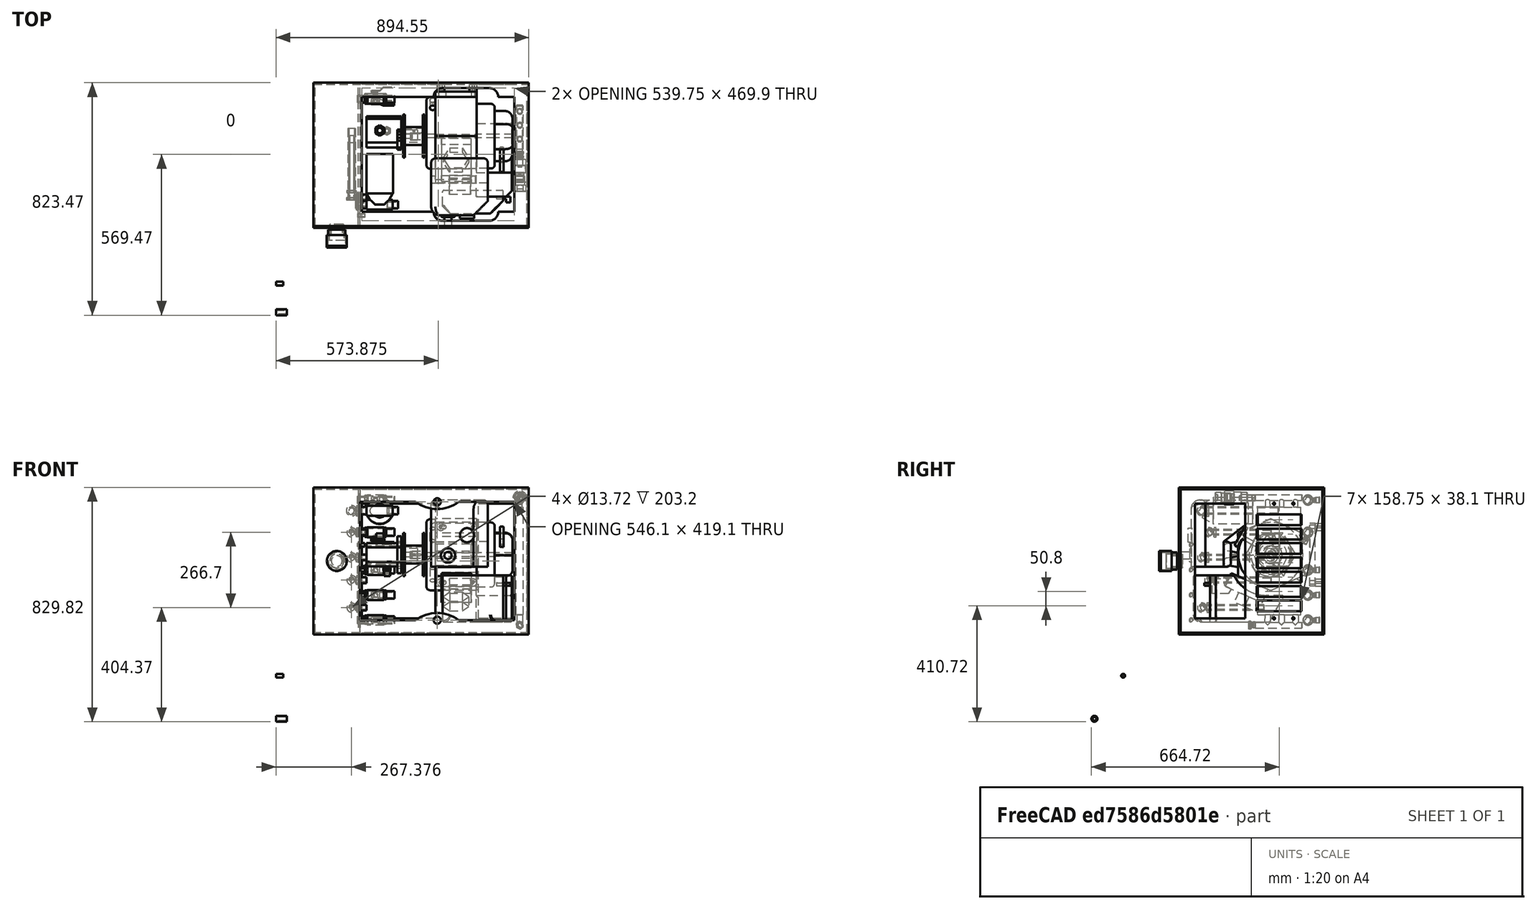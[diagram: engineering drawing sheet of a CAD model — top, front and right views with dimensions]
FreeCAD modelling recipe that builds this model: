
FCSTD DOCUMENT  (FreeCAD 0.16R6712 (Git))
Label: powercube v17.11_plumbing
License: CreativeCommons Attribution-ShareAlike
LicenseURL: http://creativecommons.org/licenses/by-sa/4.0/
objects: App::FeaturePython×29, Part::FeaturePython×17, Part::Feature×9, Part::Part2DObjectPython×4, App::DocumentObjectGroup×3
note: 30 computed .brp shape members not serialized (recipe doc carries the construction recipe); baked Part::Feature solids carry a one-line shape summary decoded from their .brp

FEATURE [Part::Feature] Cut002  label="0.75 NPT x 1.5in pipe section"
  Placement = pos=(-71.1581,-527.05,186.267) rot=(0,-1,0;1.5708rad)
  shape: bbox 38.1 x 26.67 x 26.67 mm, 4 faces (baked)
FEATURE [Part::Feature] Pad005  label="1/4" NPT pipe"
  Placement = pos=(-152.4,-203.2,-152.4) rot=(0.57735,0.57735,0.57735;2.0944rad)
  shape: bbox 25.4 x 13.72 x 13.72 mm, 4 faces (baked)
FEATURE [Part::FeaturePython] Clone039  label="Clone of 0.75 NPT x 1.5in pipe section005"  # Draft clone (typed FeaturePython)
  Objects = -> [Cut002]
  Placement = pos=(229.07,450.85,44.45) rot=(0,1,0;1.5708rad)
  Scale = (1,1,1)
FEATURE [Part::FeaturePython] Clone040  label="Clone of 0.75 NPT x 1.5in pipe section006"  # Draft clone (typed FeaturePython)
  Objects = -> [Cut002]
  Placement = pos=(229.07,450.85,133.35) rot=(0,1,0;1.5708rad)
  Scale = (1,1,1)
FEATURE [Part::FeaturePython] Clone041  label="Clone of 0.75 NPT x 1.5in pipe section007"  # Draft clone (typed FeaturePython)
  Objects = -> [Cut002]
  Placement = pos=(229.07,450.85,222.25) rot=(0,1,0;1.5708rad)
  Scale = (1,1,1)
FEATURE [Part::FeaturePython] Clone042  label="Clone of 0.75 NPT x 1.5in pipe section008"  # Draft clone (typed FeaturePython)
  Objects = -> [Cut002]
  Placement = pos=(229.07,450.85,355.6) rot=(0,1,0;1.5708rad)
  Scale = (1,1,1)
FEATURE [Part::FeaturePython] Clone043  label="Clone of 0.75 NPT x 1.5in pipe section009"  # Draft clone (typed FeaturePython)
  Objects = -> [Cut002]
  Placement = pos=(229.07,450.85,469.9) rot=(0,1,0;1.5708rad)
  Scale = (1,1,1)
FEATURE [Part::Feature] Pad006  label="engine rubber feet"
  Placement = pos=(-254,-203.2,254) rot=(1,0,0;1.5708rad)
  shape: bbox 25.4 x 25.4 x 25.4 mm, 4 faces (baked)
FEATURE [Part::FeaturePython] PC_1708_oil_filter_002  # a2plus imported part (geometry in sourceFile) (typed FeaturePython)
  Placement = pos=(214.465,115.824,431.8) rot=(1,0,0;1.5708rad)
  fixedPosition = false
  sourceFile = <userpath>/Documents/Freecad docs/Power Cube/PC_1708_oil_filter.fcstd
  timeLastImport = 0
  updateColors = true
FEATURE [Part::FeaturePython] Clone053  label="Clone of 0.75 NPT x 1.5in pipe section010"  # Draft clone (typed FeaturePython)
  Objects = -> [Cut002]
  Placement = pos=(241.77,76.2,431.8) rot=(0,1,0;1.5708rad)
  Scale = (1,1,1)
FEATURE [App::FeaturePython] circularEdgeConstraint35  label="circularEdgeConstraint35__PC_1708_oil_filter_002"  # a2plus constraint (typed FeaturePython)
  Object1 = Clone053
  Object2 = PC_1708_oil_filter_002
  SubElement1 = Edge3
  SubElement2 = Edge17
  Type = circularEdge
  directionConstraint = 0
  lockRotation = false
  offset = -19.05
FEATURE [App::FeaturePython] circularEdgeConstraint35_mirror  label="circularEdgeConstraint35__Clone of 0.75 NPT x 1.5in pipe section010"  # a2plus constraint (typed FeaturePython)
  Object1 = Clone053
  Object2 = PC_1708_oil_filter_002
  SubElement1 = Edge3
  SubElement2 = Edge17
  Type = circularEdge
  directionConstraint = 0
  lockRotation = false
  offset = -19.05
FEATURE [Part::Feature] Fusion001001  label="1240_cooler_and_fittings001"
  Placement = pos=(637.3,546.25,-104.8) rot=(0.57735,-0.57735,-0.57735;2.0944rad)
  shape: bbox 48 x 306.6 x 489 mm, 154 faces, 3 solids (baked)
FEATURE [Part::Feature] Pad001  label="0.5in x 1.5in NPT"
  Placement = pos=(-152.4,-304.8,-304.8) rot=(0.57735,0.57735,0.57735;2.0944rad)
  shape: bbox 38.1 x 21.34 x 21.34 mm, 4 faces (baked)
FEATURE [Part::FeaturePython] PC_v17_11_Frame_simple_01  # a2plus imported part (geometry in sourceFile) (typed FeaturePython)
  fixedPosition = true
  sourceFile = <userpath>/Documents/Power Cube v17.11/PC v17.11 Frame simple.fcstd
  timeLastImport = 1.53306e+09
  updateColors = true
FEATURE [App::DocumentObjectGroup] Group  label="Frame"
  Group = -> [PC_v17_11_Frame_simple_01]
FEATURE [Part::FeaturePython] Clone  label="Clone of engine rubber feet"  # Draft clone (typed FeaturePython)
  Objects = -> [Pad006]
  Placement = pos=(431,501.65,177.8) rot=(1,0,0;1.5708rad)
  Scale = (1,1,1)
FEATURE [Part::FeaturePython] Clone070  label="Clone of engine rubber feet001"  # Draft clone (typed FeaturePython)
  Objects = -> [Pad006]
  Placement = pos=(545.3,501.65,177.8) rot=(1,0,0;1.5708rad)
  Scale = (1,1,1)
FEATURE [Part::FeaturePython] Clone071  label="Clone of engine rubber feet002"  # Draft clone (typed FeaturePython)
  Objects = -> [Pad006]
  Placement = pos=(545.3,501.65,374.65) rot=(1,0,0;1.5708rad)
  Scale = (1,1,1)
FEATURE [Part::FeaturePython] Clone072  label="Clone of engine rubber feet003"  # Draft clone (typed FeaturePython)
  Objects = -> [Pad006]
  Placement = pos=(431,501.65,374.65) rot=(1,0,0;1.5708rad)
  Scale = (1,1,1)
FEATURE [App::FeaturePython] circularEdgeConstraint01  label="circularEdgeConstraint01__PC_v17_11_Frame_simple_01"  # a2plus constraint (typed FeaturePython)
  Object1 = Clone
  Object2 = PC_v17_11_Frame_simple_01
  SubElement1 = Edge5
  SubElement2 = Edge252
  Type = circularEdge
  directionConstraint = 0
  lockRotation = false
  offset = 0
FEATURE [App::FeaturePython] circularEdgeConstraint01_mirror  label="circularEdgeConstraint01__Clone of engine rubber feet"  # a2plus constraint (typed FeaturePython)
  Object1 = Clone
  Object2 = PC_v17_11_Frame_simple_01
  SubElement1 = Edge5
  SubElement2 = Edge252
  Type = circularEdge
  directionConstraint = 0
  lockRotation = false
  offset = 0
FEATURE [App::FeaturePython] circularEdgeConstraint02  label="circularEdgeConstraint02__Clone of engine rubber feet001"  # a2plus constraint (typed FeaturePython)
  Object1 = PC_v17_11_Frame_simple_01
  Object2 = Clone070
  SubElement1 = Edge249
  SubElement2 = Edge5
  Type = circularEdge
  directionConstraint = 0
  lockRotation = false
  offset = 0
FEATURE [App::FeaturePython] circularEdgeConstraint02_mirror  label="circularEdgeConstraint02__PC_v17_11_Frame_simple_01"  # a2plus constraint (typed FeaturePython)
  Object1 = PC_v17_11_Frame_simple_01
  Object2 = Clone070
  SubElement1 = Edge249
  SubElement2 = Edge5
  Type = circularEdge
  directionConstraint = 0
  lockRotation = false
  offset = 0
FEATURE [App::FeaturePython] circularEdgeConstraint03  label="circularEdgeConstraint03__PC_v17_11_Frame_simple_01"  # a2plus constraint (typed FeaturePython)
  Object1 = Clone071
  Object2 = PC_v17_11_Frame_simple_01
  SubElement1 = Edge5
  SubElement2 = Edge243
  Type = circularEdge
  directionConstraint = 0
  lockRotation = false
  offset = 0
FEATURE [App::FeaturePython] circularEdgeConstraint03_mirror  label="circularEdgeConstraint03__Clone of engine rubber feet002"  # a2plus constraint (typed FeaturePython)
  Object1 = Clone071
  Object2 = PC_v17_11_Frame_simple_01
  SubElement1 = Edge5
  SubElement2 = Edge243
  Type = circularEdge
  directionConstraint = 0
  lockRotation = false
  offset = 0
FEATURE [App::FeaturePython] circularEdgeConstraint04  label="circularEdgeConstraint04__Clone of engine rubber feet003"  # a2plus constraint (typed FeaturePython)
  Object1 = PC_v17_11_Frame_simple_01
  Object2 = Clone072
  SubElement1 = Edge246
  SubElement2 = Edge5
  Type = circularEdge
  directionConstraint = 0
  lockRotation = false
  offset = 0
FEATURE [App::FeaturePython] circularEdgeConstraint04_mirror  label="circularEdgeConstraint04__PC_v17_11_Frame_simple_01"  # a2plus constraint (typed FeaturePython)
  Object1 = PC_v17_11_Frame_simple_01
  Object2 = Clone072
  SubElement1 = Edge246
  SubElement2 = Edge5
  Type = circularEdge
  directionConstraint = 0
  lockRotation = false
  offset = 0
FEATURE [App::DocumentObjectGroup] Group001  label="Power"
  Group = -> [Pad006,Clone,Clone070,Clone071,Clone072,circularEdgeConstraint01,circularEdgeConstraint02_mirror,circularEdgeConstraint03,circularEdgeConstraint04_mirror]
FEATURE [App::FeaturePython] circularEdgeConstraint06_mirror  label="circularEdgeConstraint06__Clone of 1/4" NPT pipe"  # a2plus constraint (typed FeaturePython)
  Object1 = Clone073
  Object2 = PC_v17_11_Frame_simple_01
  SubElement1 = Edge6
  SubElement2 = Edge81
  Type = circularEdge
  directionConstraint = 1
  lockRotation = false
  offset = 0
FEATURE [App::DocumentObjectGroup] Group002  label="Plumbing"
  Group = -> [Pad001,Fusion001001,Cut002,Pad005,Clone039,Clone040,Clone041,Clone042,Clone043,PC_1708_oil_filter_002,Clone053,circularEdgeConstraint35,circularEdgeConstraint06_mirror]
FEATURE [Part::Feature] Compound002001  label="0.75in NPT Ball Valve"
  Placement = pos=(812.8,-175.26,330.2) rot=(-0.57735,-0.57735,-0.57735;2.0944rad)
  shape: bbox 104 x 60.2 x 35.56 mm, 53 faces, 5 solids (baked)
FEATURE [Part::FeaturePython] Clone077  label="Clone of 0.75in NPT Ball Valve"  # Draft clone (typed FeaturePython)
  Objects = -> [Compound002001]
  Placement = pos=(237.96,440.69,44.45) rot=(0.57735,0.57735,0.57735;4.18879rad)
  Scale = (1,1,1)
FEATURE [Part::FeaturePython] Clone078  label="Clone of 0.75in NPT Ball Valve001"  # Draft clone (typed FeaturePython)
  Objects = -> [Compound002001]
  Placement = pos=(237.96,440.69,133.35) rot=(0.57735,0.57735,0.57735;4.18879rad)
  Scale = (1,1,1)
FEATURE [Part::FeaturePython] Clone079  label="Clone of 0.75in NPT Ball Valve002"  # Draft clone (typed FeaturePython)
  Objects = -> [Compound002001]
  Placement = pos=(237.96,440.69,222.25) rot=(0.57735,0.57735,0.57735;4.18879rad)
  Scale = (1,1,1)
FEATURE [Part::FeaturePython] Clone080  label="Clone of 0.75in NPT Ball Valve003"  # Draft clone (typed FeaturePython)
  Objects = -> [Compound002001]
  Placement = pos=(237.96,454.305,365.155) rot=(0.701739,0.701739,-0.122979;2.89686rad)
  Scale = (1,1,1)
FEATURE [Part::FeaturePython] Clone081  label="Clone of 0.75in NPT Ball Valve004"  # Draft clone (typed FeaturePython)
  Objects = -> [Compound002001]
  Placement = pos=(237.96,440.69,469.9) rot=(0.57735,0.57735,0.57735;4.18879rad)
  Scale = (1,1,1)
FEATURE [App::FeaturePython] circularEdgeConstraint26  # a2plus constraint (typed FeaturePython)
  Object1 = Clone039
  Object2 = Clone077
  SubElement1 = Edge3
  SubElement2 = Edge59
  Type = circularEdge
  directionConstraint = 0
  lockRotation = false
  offset = -8.89
FEATURE [App::FeaturePython] circularEdgeConstraint27  # a2plus constraint (typed FeaturePython)
  Object1 = Clone040
  Object2 = Clone078
  SubElement1 = Edge3
  SubElement2 = Edge59
  Type = circularEdge
  directionConstraint = 0
  lockRotation = false
  offset = -8.89
FEATURE [App::FeaturePython] circularEdgeConstraint28  # a2plus constraint (typed FeaturePython)
  Object1 = Clone041
  Object2 = Clone079
  SubElement1 = Edge3
  SubElement2 = Edge59
  Type = circularEdge
  directionConstraint = 0
  lockRotation = false
  offset = -8.89
FEATURE [App::FeaturePython] circularEdgeConstraint30  # a2plus constraint (typed FeaturePython)
  Object1 = Clone043
  Object2 = Clone081
  SubElement1 = Edge3
  SubElement2 = Edge59
  Type = circularEdge
  directionConstraint = 0
  lockRotation = false
  offset = -8.89
FEATURE [Part::Feature] Compound002002002005003  label="engine_pump_module"
  Placement = pos=(297.65,744.033,-100.328) rot=(0,0,1;0rad)
  shape: bbox 517.5 x 482.5 x 432.2 mm, 345 faces, 25 solids (baked)
FEATURE [App::FeaturePython] circularEdgeConstraint05  label="cEc05_engine_module_vertical"  # a2plus constraint (typed FeaturePython)
  Object1 = Compound002002002005003
  Object2 = Clone071
  SubElement1 = Edge773
  SubElement2 = Edge6
  Type = circularEdge
  directionConstraint = 1
  lockRotation = false
  offset = 0
FEATURE [App::FeaturePython] circularEdgeConstraint06  label="circularEdgeConstraint06__PC_v17_11_Frame_simple_01"  # a2plus constraint (typed FeaturePython)
  Object1 = Clone081
  Object2 = PC_v17_11_Frame_simple_01
  SubElement1 = Edge72
  SubElement2 = Edge91
  Type = circularEdge
  directionConstraint = 0
  lockRotation = false
  offset = -12.7
FEATURE [App::FeaturePython] circularEdgeConstraint06_mirror001  label="circularEdgeConstraint06__Clone of 0.75in NPT Ball Valve004"  # a2plus constraint (typed FeaturePython)
  Object1 = Clone081
  Object2 = PC_v17_11_Frame_simple_01
  SubElement1 = Edge72
  SubElement2 = Edge91
  Type = circularEdge
  directionConstraint = 0
  lockRotation = false
  offset = -12.7
FEATURE [App::FeaturePython] circularEdgeConstraint07  label="circularEdgeConstraint07__PC_v17_11_Frame_simple_01"  # a2plus constraint (typed FeaturePython)
  Object1 = Clone077
  Object2 = PC_v17_11_Frame_simple_01
  SubElement1 = Edge72
  SubElement2 = Edge31
  Type = circularEdge
  directionConstraint = 0
  lockRotation = false
  offset = -12.7
FEATURE [App::FeaturePython] circularEdgeConstraint07_mirror  label="circularEdgeConstraint07__Clone of 0.75in NPT Ball Valve"  # a2plus constraint (typed FeaturePython)
  Object1 = Clone077
  Object2 = PC_v17_11_Frame_simple_01
  SubElement1 = Edge72
  SubElement2 = Edge31
  Type = circularEdge
  directionConstraint = 0
  lockRotation = false
  offset = -12.7
FEATURE [App::FeaturePython] circularEdgeConstraint08  label="circularEdgeConstraint08__PC_v17_11_Frame_simple_01"  # a2plus constraint (typed FeaturePython)
  Object1 = Clone078
  Object2 = PC_v17_11_Frame_simple_01
  SubElement1 = Edge72
  SubElement2 = Edge73
  Type = circularEdge
  directionConstraint = 0
  lockRotation = false
  offset = -12.7
FEATURE [App::FeaturePython] circularEdgeConstraint08_mirror  label="circularEdgeConstraint08__Clone of 0.75in NPT Ball Valve001"  # a2plus constraint (typed FeaturePython)
  Object1 = Clone078
  Object2 = PC_v17_11_Frame_simple_01
  SubElement1 = Edge72
  SubElement2 = Edge73
  Type = circularEdge
  directionConstraint = 0
  lockRotation = false
  offset = -12.7
FEATURE [App::FeaturePython] circularEdgeConstraint09  label="circularEdgeConstraint09__PC_v17_11_Frame_simple_01"  # a2plus constraint (typed FeaturePython)
  Object1 = Clone079
  Object2 = PC_v17_11_Frame_simple_01
  SubElement1 = Edge72
  SubElement2 = Edge79
  Type = circularEdge
  directionConstraint = 0
  lockRotation = false
  offset = -12.7
FEATURE [App::FeaturePython] circularEdgeConstraint09_mirror  label="circularEdgeConstraint09__Clone of 0.75in NPT Ball Valve002"  # a2plus constraint (typed FeaturePython)
  Object1 = Clone079
  Object2 = PC_v17_11_Frame_simple_01
  SubElement1 = Edge72
  SubElement2 = Edge79
  Type = circularEdge
  directionConstraint = 0
  lockRotation = false
  offset = -12.7
FEATURE [App::FeaturePython] circularEdgeConstraint10  label="circularEdgeConstraint10__PC_v17_11_Frame_simple_01"  # a2plus constraint (typed FeaturePython)
  Object1 = Clone080
  Object2 = PC_v17_11_Frame_simple_01
  SubElement1 = Edge72
  SubElement2 = Edge85
  Type = circularEdge
  directionConstraint = 0
  lockRotation = false
  offset = -12.7
FEATURE [App::FeaturePython] circularEdgeConstraint10_mirror  label="circularEdgeConstraint10__Clone of 0.75in NPT Ball Valve003"  # a2plus constraint (typed FeaturePython)
  Object1 = Clone080
  Object2 = PC_v17_11_Frame_simple_01
  SubElement1 = Edge72
  SubElement2 = Edge85
  Type = circularEdge
  directionConstraint = 0
  lockRotation = false
  offset = -12.7
FEATURE [App::FeaturePython] circularEdgeConstraint11  label="circularEdgeConstraint11_valve_out_"  # a2plus constraint (typed FeaturePython)
  Object1 = Clone042
  Object2 = Clone080
  SubElement1 = Edge3
  SubElement2 = Edge59
  Type = circularEdge
  directionConstraint = 0
  lockRotation = false
  offset = -8.89
FEATURE [Part::Feature] Compound001  label="SAE -12 to 3/4" adapter"
  Placement = pos=(163.889,288.901,412.982) rot=(0,0.999967,-0.008118;1.5708rad)
  shape: bbox 31.9 x 36.73 x 47.21 mm, 17 faces, 3 solids (baked)
FEATURE [App::FeaturePython] circularEdgeConstraint12  # a2plus constraint (typed FeaturePython)
  Object1 = Compound001
  Object2 = Compound002002002005003
  SubElement1 = Edge30
  SubElement2 = Edge88
  Type = circularEdge
  directionConstraint = 1
  lockRotation = false
  offset = 0
FEATURE [Part::Feature] Compound002002002005004  label="SAE 10 x 0.5in NPT"
  Placement = pos=(291.711,286.684,139.941) rot=(0,-0.999967,0.008118;1.5708rad)
  shape: bbox 25.52 x 29.4 x 47.17 mm, 17 faces, 3 solids (baked)
FEATURE [App::FeaturePython] circularEdgeConstraint13  # a2plus constraint (typed FeaturePython)
  Object1 = Compound002002002005004
  Object2 = Compound002002002005003
  SubElement1 = Edge30
  SubElement2 = Edge93
  Type = circularEdge
  directionConstraint = 1
  lockRotation = false
  offset = 0
FEATURE [Part::Part2DObjectPython] Circle001  # Draft 2D object (typed FeaturePython)
  FirstAngle = 0
  LastAngle = 0
  MakeFace = false
  Placement = pos=(267.17,450.85,44.45) rot=(0.57735,0.57735,0.57735;2.0944rad)
  Radius = 13.335
  Support = -> Clone039
FEATURE [Part::Part2DObjectPython] Circle002  # Draft 2D object (typed FeaturePython)
  FirstAngle = 0
  LastAngle = 0
  MakeFace = false
  Placement = pos=(267.17,450.85,44.45) rot=(0.57735,0.57735,0.57735;2.0944rad)
  Radius = 15.875
FEATURE [Part::Part2DObjectPython] DWire  # Draft 2D object (typed FeaturePython)
  ChamferSize = 0
  Closed = false
  End = (276.114,424.155,458.787)
  FilletRadius = 0
  Length = 967.963
  MakeFace = true
  Points = (20) [(267.355,451.734,44.45),(283.323,451.734,44.45),(317.362,451.734,44.45),(328.179,451.734,44.45),(342.1,451.734,44.45),(342.1,451.734,91.1356),+14 more]
  Start = (267.355,451.734,44.45)
  Subdivisions = 10
FEATURE [Part::Part2DObjectPython] BSpline  # Draft 2D object (typed FeaturePython)
  Closed = false
  MakeFace = true
  Points = (4) [(267.355,451.734,44.45),(283.323,451.734,44.45),(342.1,451.734,44.45),(342.1,451.734,91.1356)]
